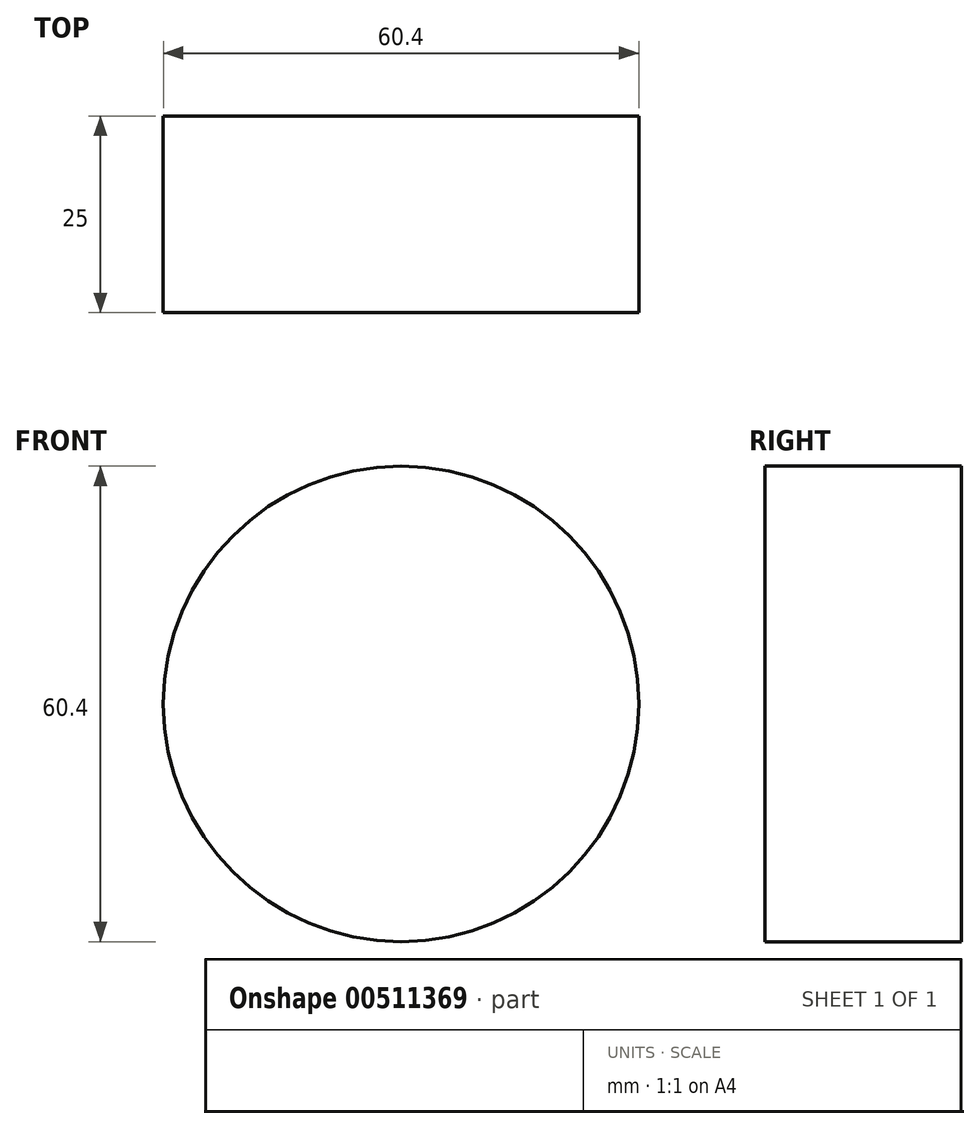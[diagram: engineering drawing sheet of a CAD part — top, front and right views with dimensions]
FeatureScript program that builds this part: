
annotation { "Feature Type Name" : "Feature", "Feature Type Description" : "" }
export const myFeature = defineFeature(function(context is Context, id is Id, definition is map)
    precondition{}
    {
        {
            var Q0;
            Q0=qCreatedBy(makeId("Front.planeOp"),FACE);
            var sketch = newSketch(context, id + "F0", { "sketchPlane" : qUnion([Q0])});
            skCircle(sketch, "E0", {"center": v(0, 0) * mm, "radius": 30.2 * mm});
            skSolve(sketch);
        }
        {
            var Q0;
            Q0=makeQuery(id+"F0.imprint","IMPRINT",FACE,{"disambiguationData":[TD([[makeQuery(id+"F0.imprint","IMPRINT",EDGE,{"derivedFrom":sQuery(id+"F0.wireOp",EDGE,"E0")}),1.0]])]});
            extrude(context, id + "F1", {"entities" : qUnion([Q0]), "oppositeDirection" : true, "depth" : 25 * mm});
        }
    });
